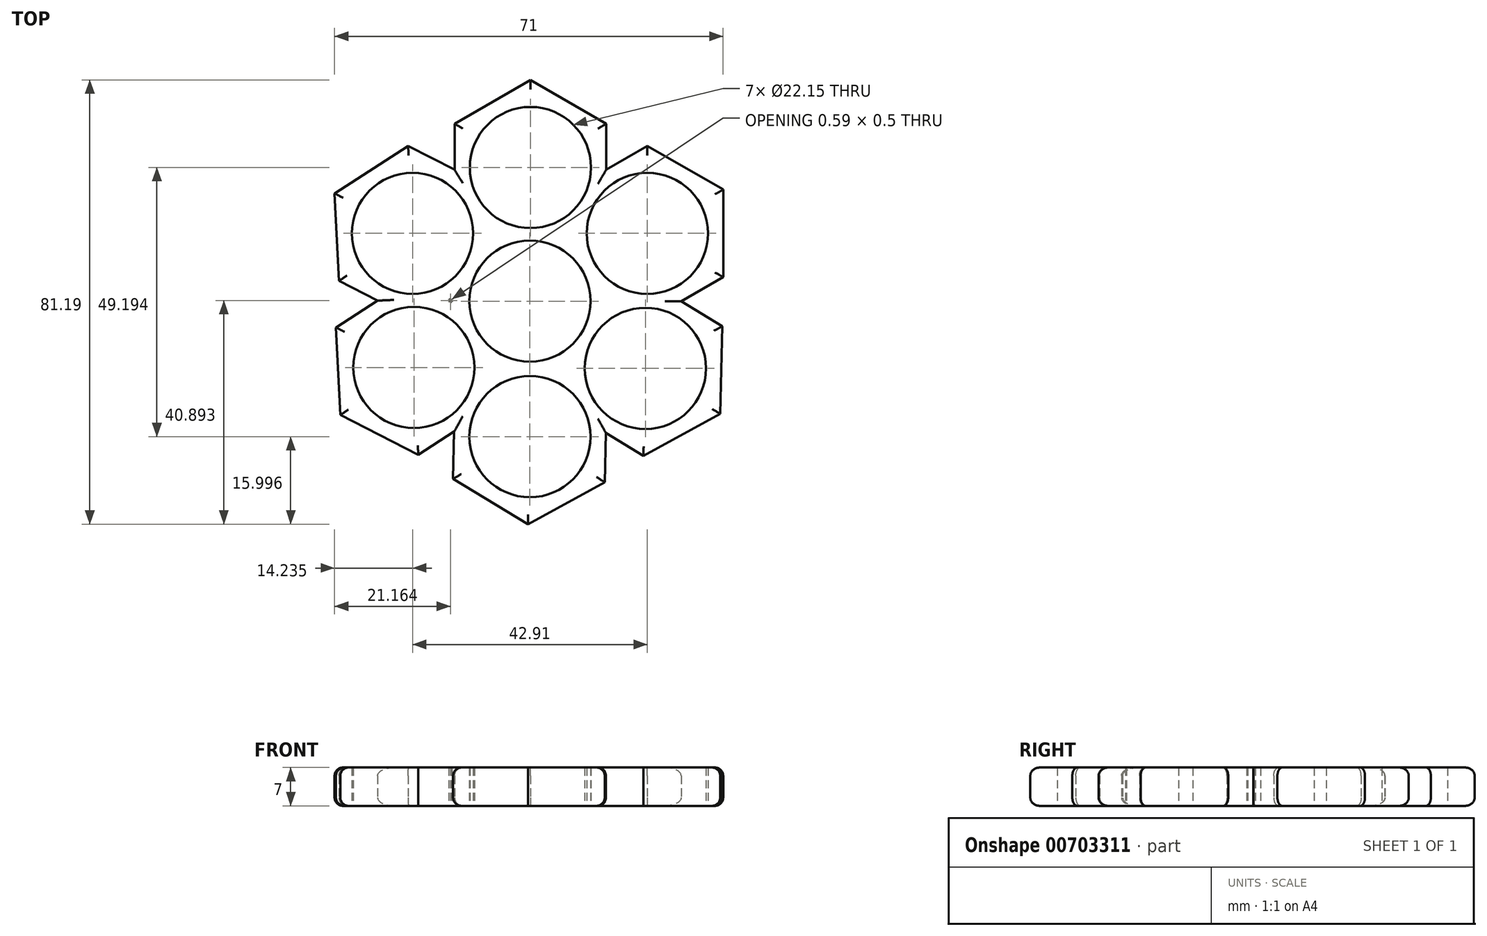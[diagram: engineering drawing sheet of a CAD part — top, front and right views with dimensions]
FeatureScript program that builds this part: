
annotation { "Feature Type Name" : "Feature", "Feature Type Description" : "" }
export const myFeature = defineFeature(function(context is Context, id is Id, definition is map)
    precondition{}
    {
        {
            var Q0;
            Q0=qCreatedBy(makeId("Top.planeOp"),FACE);
            var sketch = newSketch(context, id + "F0", { "sketchPlane" : qUnion([Q0])});
            skCircle(sketch, "E0.cCircle", {"center": v(0, 0) * mm, "radius": 12.21 * mm, "construction": true});
            skLineSegment(sketch, "E0.0", {"start": v(0.1, 24.42) * mm, "end": v(21.1, -12.3) * mm});
            skLineSegment(sketch, "E0.1", {"start": v(21.1, -12.3) * mm, "end": v(-21.2, -12.13) * mm});
            skLineSegment(sketch, "E0.2", {"start": v(-21.2, -12.13) * mm, "end": v(0.1, 24.42) * mm});
            skPoint(sketch, "E0.0.midPoint", {"position": v(10.6, 6.06) * mm});
            skCircle(sketch, "E1.cCircle", {"center": v(0.1, 24.42) * mm, "radius": 13.86 * mm, "construction": true});
            skLineSegment(sketch, "E1.0", {"start": v(13.95, 32.42) * mm, "end": v(13.95, 16.42) * mm});
            skLineSegment(sketch, "E1.1", {"start": v(13.95, 16.42) * mm, "end": v(0.1, 8.42) * mm});
            skLineSegment(sketch, "E1.2", {"start": v(0.1, 8.42) * mm, "end": v(-13.76, 16.42) * mm});
            skLineSegment(sketch, "E1.3", {"start": v(-13.76, 16.42) * mm, "end": v(-13.76, 32.42) * mm});
            skLineSegment(sketch, "E1.4", {"start": v(-13.76, 32.42) * mm, "end": v(0.1, 40.42) * mm});
            skLineSegment(sketch, "E1.5", {"start": v(0.1, 40.42) * mm, "end": v(13.95, 32.42) * mm});
            skPoint(sketch, "E1.0.midPoint", {"position": v(13.95, 24.42) * mm});
            skCircle(sketch, "E2.cCircle", {"center": v(21.1, -12.3) * mm, "radius": 13.86 * mm, "construction": true});
            skLineSegment(sketch, "E2.0", {"start": v(35.14, -4.61) * mm, "end": v(34.77, -20.6) * mm});
            skLineSegment(sketch, "E2.1", {"start": v(34.77, -20.6) * mm, "end": v(20.74, -28.29) * mm});
            skLineSegment(sketch, "E2.2", {"start": v(20.74, -28.29) * mm, "end": v(7.07, -19.98) * mm});
            skLineSegment(sketch, "E2.3", {"start": v(7.07, -19.98) * mm, "end": v(7.43, -3.98) * mm});
            skLineSegment(sketch, "E2.4", {"start": v(7.43, -3.98) * mm, "end": v(21.46, 3.7) * mm});
            skLineSegment(sketch, "E2.5", {"start": v(21.46, 3.7) * mm, "end": v(35.14, -4.61) * mm});
            skPoint(sketch, "E2.0.midPoint", {"position": v(34.95, -12.6) * mm});
            skCircle(sketch, "E3.cCircle", {"center": v(-21.2, -12.13) * mm, "radius": 13.86 * mm, "construction": true});
            skLineSegment(sketch, "E3.0", {"start": v(-20.4, -28.1) * mm, "end": v(-34.64, -20.8) * mm});
            skLineSegment(sketch, "E3.1", {"start": v(-34.64, -20.8) * mm, "end": v(-35.43, -4.83) * mm});
            skLineSegment(sketch, "E3.2", {"start": v(-35.43, -4.83) * mm, "end": v(-22, 3.85) * mm});
            skLineSegment(sketch, "E3.3", {"start": v(-22, 3.85) * mm, "end": v(-7.76, -3.45) * mm});
            skLineSegment(sketch, "E3.4", {"start": v(-7.76, -3.45) * mm, "end": v(-6.96, -19.43) * mm});
            skLineSegment(sketch, "E3.5", {"start": v(-6.96, -19.43) * mm, "end": v(-20.4, -28.1) * mm});
            skPoint(sketch, "E3.0.midPoint", {"position": v(-27.52, -24.46) * mm});
            skCircle(sketch, "E4", {"center": v(0.1, 24.42) * mm, "radius": 11.07 * mm});
            skCircle(sketch, "E5", {"center": v(0, 0) * mm, "radius": 11.07 * mm});
            skCircle(sketch, "E6", {"center": v(-21.2, -12.13) * mm, "radius": 11.07 * mm});
            skCircle(sketch, "E7", {"center": v(21.1, -12.3) * mm, "radius": 11.07 * mm});
            skCircle(sketch, "E8.cCircle", {"center": v(0, 0) * mm, "radius": 12.39 * mm, "construction": true});
            skLineSegment(sketch, "E8.0", {"start": v(21.45, 12.39) * mm, "end": v(0, -24.77) * mm});
            skLineSegment(sketch, "E8.1", {"start": v(0, -24.77) * mm, "end": v(-21.45, 12.39) * mm});
            skLineSegment(sketch, "E8.2", {"start": v(-21.45, 12.39) * mm, "end": v(21.45, 12.39) * mm});
            skPoint(sketch, "E8.0.midPoint", {"position": v(10.73, -6.2) * mm});
            skCircle(sketch, "E9.cCircle", {"center": v(21.45, 12.39) * mm, "radius": 13.86 * mm, "construction": true});
            skLineSegment(sketch, "E9.0", {"start": v(35.31, 4.39) * mm, "end": v(21.45, -3.61) * mm});
            skLineSegment(sketch, "E9.1", {"start": v(21.45, -3.61) * mm, "end": v(7.6, 4.39) * mm});
            skLineSegment(sketch, "E9.2", {"start": v(7.6, 4.39) * mm, "end": v(7.6, 20.39) * mm});
            skLineSegment(sketch, "E9.3", {"start": v(7.6, 20.39) * mm, "end": v(21.45, 28.39) * mm});
            skLineSegment(sketch, "E9.4", {"start": v(21.45, 28.39) * mm, "end": v(35.31, 20.39) * mm});
            skLineSegment(sketch, "E9.5", {"start": v(35.31, 20.39) * mm, "end": v(35.31, 4.39) * mm});
            skPoint(sketch, "E9.0.midPoint", {"position": v(28.38, 0.39) * mm});
            skCircle(sketch, "E10.cCircle", {"center": v(0, -24.77) * mm, "radius": 13.86 * mm, "construction": true});
            skLineSegment(sketch, "E10.0", {"start": v(13.67, -33.09) * mm, "end": v(-0.36, -40.77) * mm});
            skLineSegment(sketch, "E10.1", {"start": v(-0.36, -40.77) * mm, "end": v(-14.03, -32.46) * mm});
            skLineSegment(sketch, "E10.2", {"start": v(-14.03, -32.46) * mm, "end": v(-13.67, -16.46) * mm});
            skLineSegment(sketch, "E10.3", {"start": v(-13.67, -16.46) * mm, "end": v(0.36, -8.78) * mm});
            skLineSegment(sketch, "E10.4", {"start": v(0.36, -8.78) * mm, "end": v(14.03, -17.1) * mm});
            skLineSegment(sketch, "E10.5", {"start": v(14.03, -17.1) * mm, "end": v(13.67, -33.09) * mm});
            skPoint(sketch, "E10.0.midPoint", {"position": v(6.65, -36.93) * mm});
            skCircle(sketch, "E11.cCircle", {"center": v(-21.45, 12.39) * mm, "radius": 13.86 * mm, "construction": true});
            skLineSegment(sketch, "E11.0", {"start": v(-34.9, 3.7) * mm, "end": v(-35.7, 19.69) * mm});
            skLineSegment(sketch, "E11.1", {"start": v(-35.7, 19.69) * mm, "end": v(-22.25, 28.37) * mm});
            skLineSegment(sketch, "E11.2", {"start": v(-22.25, 28.37) * mm, "end": v(-8.01, 21.07) * mm});
            skLineSegment(sketch, "E11.3", {"start": v(-8.01, 21.07) * mm, "end": v(-7.22, 5.09) * mm});
            skLineSegment(sketch, "E11.4", {"start": v(-7.22, 5.09) * mm, "end": v(-20.66, -3.6) * mm});
            skLineSegment(sketch, "E11.5", {"start": v(-20.66, -3.6) * mm, "end": v(-34.9, 3.7) * mm});
            skPoint(sketch, "E11.0.midPoint", {"position": v(-35.3, 11.7) * mm});
            skCircle(sketch, "E12", {"center": v(21.45, 12.39) * mm, "radius": 11.07 * mm});
            skCircle(sketch, "E13", {"center": v(-21.45, 12.39) * mm, "radius": 11.07 * mm});
            skCircle(sketch, "E14", {"center": v(0, -24.77) * mm, "radius": 11.07 * mm});
            skSolve(sketch);
        }
        {
            var Q0;
            {var subQ16=sQuery(id+"F0.wireOp",EDGE,"E11.0");Q0=makeQuery(id+"F0.imprint","IMPRINT",FACE,{"disambiguationData":[TD([[makeQuery(id+"F0.imprint","IMPRINT",EDGE,{"derivedFrom":subQ16}),-1.0]])]});}
            var Q1;
            {var subQ7=sQuery(id+"F0.wireOp",EDGE,"E0.2");var subQ9=sQuery(id+"F0.wireOp",EDGE,"E11.4");var subQ11=makeQuery(id+"F0.imprint","INTERSECT",VERTEX,{"derivedFrom":[subQ7,subQ9]});Q1=makeQuery(id+"F0.imprint","IMPRINT",FACE,{"disambiguationData":[TD([[makeQuery(id+"F0.imprint","IMPRINT",EDGE,{"disambiguationData":[TD([[subQ11,-1.0]])],"derivedFrom":subQ7}),1.0]])]});}
            var Q2;
            {var subQ6=sQuery(id+"F0.wireOp",EDGE,"E1.4");Q2=makeQuery(id+"F0.imprint","IMPRINT",FACE,{"disambiguationData":[TD([[makeQuery(id+"F0.imprint","IMPRINT",EDGE,{"derivedFrom":subQ6}),-1.0]])]});}
            var Q3;
            {var subQ5=sQuery(id+"F0.wireOp",EDGE,"E4");var subQ6=sQuery(id+"F0.wireOp",EDGE,"E0.0");var subQ7=makeQuery(id+"F0.imprint","INTERSECT",VERTEX,{"derivedFrom":[subQ6,subQ5]});Q3=makeQuery(id+"F0.imprint","IMPRINT",FACE,{"disambiguationData":[TD([[makeQuery(id+"F0.imprint","IMPRINT",EDGE,{"disambiguationData":[TD([[subQ7,-1.0]])],"derivedFrom":subQ6}),-1.0]])]});}
            var Q4;
            Q4=makeQuery(id+"F0.imprint","IMPRINT",FACE,{"disambiguationData":[TD([[makeQuery(id+"F0.imprint","IMPRINT",EDGE,{"derivedFrom":sQuery(id+"F0.wireOp",EDGE,"E5")}),-1.0]])]});
            var Q5;
            {var subQ0=sQuery(id+"F0.wireOp",EDGE,"E1.1");var subQ1=sQuery(id+"F0.wireOp",EDGE,"E0.0");var subQ2=makeQuery(id+"F0.imprint","INTERSECT",VERTEX,{"derivedFrom":[subQ1,subQ0]});Q5=makeQuery(id+"F0.imprint","IMPRINT",FACE,{"disambiguationData":[TD([[makeQuery(id+"F0.imprint","IMPRINT",EDGE,{"disambiguationData":[TD([[subQ2,-1.0]])],"derivedFrom":subQ1}),1.0]])]});}
            var Q6;
            {var subQ1=sQuery(id+"F0.wireOp",EDGE,"E0.0");var subQ7=sQuery(id+"F0.wireOp",EDGE,"E9.2");var subQ8=makeQuery(id+"F0.imprint","INTERSECT",VERTEX,{"derivedFrom":[subQ1,subQ7]});Q6=makeQuery(id+"F0.imprint","IMPRINT",FACE,{"disambiguationData":[TD([[makeQuery(id+"F0.imprint","IMPRINT",EDGE,{"disambiguationData":[TD([[subQ8,-1.0]])],"derivedFrom":subQ1}),1.0]])]});}
            var Q7;
            {var subQ21=sQuery(id+"F0.wireOp",EDGE,"E9.4");Q7=makeQuery(id+"F0.imprint","IMPRINT",FACE,{"disambiguationData":[TD([[makeQuery(id+"F0.imprint","IMPRINT",EDGE,{"derivedFrom":subQ21}),-1.0]])]});}
            var Q8;
            {var subQ5=sQuery(id+"F0.wireOp",EDGE,"E11.5");var subQ9=sQuery(id+"F0.wireOp",EDGE,"E3.2");var subQ10=makeQuery(id+"F0.imprint","INTERSECT",VERTEX,{"derivedFrom":[subQ9,subQ5]});Q8=makeQuery(id+"F0.imprint","IMPRINT",FACE,{"disambiguationData":[TD([[makeQuery(id+"F0.imprint","IMPRINT",EDGE,{"disambiguationData":[TD([[subQ10,-1.0]])],"derivedFrom":subQ9}),-1.0]])]});}
            var Q9;
            {var subQ0=sQuery(id+"F0.wireOp",EDGE,"E13");var subQ1=sQuery(id+"F0.wireOp",EDGE,"E3.3");var subQ2=makeQuery(id+"F0.imprint","INTERSECT",VERTEX,{"derivedFrom":[subQ1,subQ0]});Q9=makeQuery(id+"F0.imprint","IMPRINT",FACE,{"disambiguationData":[TD([[makeQuery(id+"F0.imprint","IMPRINT",EDGE,{"disambiguationData":[TD([[subQ2,-1.0]])],"derivedFrom":subQ1}),1.0]])]});}
            var Q10;
            {var subQ0=sQuery(id+"F0.wireOp",EDGE,"E11.4");var subQ1=sQuery(id+"F0.wireOp",EDGE,"E0.2");var subQ2=makeQuery(id+"F0.imprint","INTERSECT",VERTEX,{"derivedFrom":[subQ1,subQ0]});Q10=makeQuery(id+"F0.imprint","IMPRINT",FACE,{"disambiguationData":[TD([[makeQuery(id+"F0.imprint","IMPRINT",EDGE,{"disambiguationData":[TD([[subQ2,-1.0]])],"derivedFrom":subQ1}),-1.0]])]});}
            var Q11;
            {var subQ0=sQuery(id+"F0.wireOp",EDGE,"E8.2");var subQ1=sQuery(id+"F0.wireOp",EDGE,"E0.2");var subQ2=makeQuery(id+"F0.imprint","INTERSECT",VERTEX,{"derivedFrom":[subQ1,subQ0]});Q11=makeQuery(id+"F0.imprint","IMPRINT",FACE,{"disambiguationData":[TD([[makeQuery(id+"F0.imprint","IMPRINT",EDGE,{"disambiguationData":[TD([[subQ2,-1.0]])],"derivedFrom":subQ1}),1.0]])]});}
            var Q12;
            {var subQ0=sQuery(id+"F0.wireOp",EDGE,"E8.2");var subQ1=sQuery(id+"F0.wireOp",EDGE,"E0.0");var subQ2=makeQuery(id+"F0.imprint","INTERSECT",VERTEX,{"derivedFrom":[subQ1,subQ0]});Q12=makeQuery(id+"F0.imprint","IMPRINT",FACE,{"disambiguationData":[TD([[makeQuery(id+"F0.imprint","IMPRINT",EDGE,{"disambiguationData":[TD([[subQ2,-1.0]])],"derivedFrom":subQ1}),1.0]])]});}
            var Q13;
            {var subQ0=sQuery(id+"F0.wireOp",EDGE,"E1.1");var subQ1=sQuery(id+"F0.wireOp",EDGE,"E0.0");var subQ2=makeQuery(id+"F0.imprint","INTERSECT",VERTEX,{"derivedFrom":[subQ1,subQ0]});Q13=makeQuery(id+"F0.imprint","IMPRINT",FACE,{"disambiguationData":[TD([[makeQuery(id+"F0.imprint","IMPRINT",EDGE,{"disambiguationData":[TD([[subQ2,-1.0]])],"derivedFrom":subQ1}),-1.0]])]});}
            var Q14;
            {var subQ0=sQuery(id+"F0.wireOp",EDGE,"E8.2");var subQ1=sQuery(id+"F0.wireOp",EDGE,"E0.2");var subQ2=makeQuery(id+"F0.imprint","INTERSECT",VERTEX,{"derivedFrom":[subQ1,subQ0]});Q14=makeQuery(id+"F0.imprint","IMPRINT",FACE,{"disambiguationData":[TD([[makeQuery(id+"F0.imprint","IMPRINT",EDGE,{"disambiguationData":[TD([[subQ2,-1.0]])],"derivedFrom":subQ1}),-1.0]])]});}
            var Q15;
            {var subQ0=sQuery(id+"F0.wireOp",EDGE,"E11.3");var subQ1=sQuery(id+"F0.wireOp",EDGE,"E0.2");var subQ2=makeQuery(id+"F0.imprint","INTERSECT",VERTEX,{"derivedFrom":[subQ1,subQ0]});Q15=makeQuery(id+"F0.imprint","IMPRINT",FACE,{"disambiguationData":[TD([[makeQuery(id+"F0.imprint","IMPRINT",EDGE,{"disambiguationData":[TD([[subQ2,-1.0]])],"derivedFrom":subQ1}),1.0]])]});}
            var Q16;
            {var subQ0=sQuery(id+"F0.wireOp",EDGE,"E9.2");var subQ1=sQuery(id+"F0.wireOp",EDGE,"E0.0");var subQ2=makeQuery(id+"F0.imprint","INTERSECT",VERTEX,{"derivedFrom":[subQ1,subQ0]});Q16=makeQuery(id+"F0.imprint","IMPRINT",FACE,{"disambiguationData":[TD([[makeQuery(id+"F0.imprint","IMPRINT",EDGE,{"disambiguationData":[TD([[subQ2,-1.0]])],"derivedFrom":subQ1}),-1.0]])]});}
            var Q17;
            {var subQ0=sQuery(id+"F0.wireOp",EDGE,"E9.1");var subQ1=sQuery(id+"F0.wireOp",EDGE,"E0.0");var subQ2=makeQuery(id+"F0.imprint","INTERSECT",VERTEX,{"derivedFrom":[subQ1,subQ0]});Q17=makeQuery(id+"F0.imprint","IMPRINT",FACE,{"disambiguationData":[TD([[makeQuery(id+"F0.imprint","IMPRINT",EDGE,{"disambiguationData":[TD([[subQ2,-1.0]])],"derivedFrom":subQ1}),1.0]])]});}
            var Q18;
            {var subQ0=sQuery(id+"F0.wireOp",EDGE,"E2.4");var subQ1=sQuery(id+"F0.wireOp",EDGE,"E0.0");var subQ2=makeQuery(id+"F0.imprint","INTERSECT",VERTEX,{"derivedFrom":[subQ1,subQ0]});Q18=makeQuery(id+"F0.imprint","IMPRINT",FACE,{"disambiguationData":[TD([[makeQuery(id+"F0.imprint","IMPRINT",EDGE,{"disambiguationData":[TD([[subQ2,-1.0]])],"derivedFrom":subQ1}),-1.0]])]});}
            var Q19;
            {var subQ15=sQuery(id+"F0.wireOp",EDGE,"E2.0");Q19=makeQuery(id+"F0.imprint","IMPRINT",FACE,{"disambiguationData":[TD([[makeQuery(id+"F0.imprint","IMPRINT",EDGE,{"derivedFrom":subQ15}),-1.0]])]});}
            var Q20;
            {var subQ0=sQuery(id+"F0.wireOp",EDGE,"E8.0");var subQ1=sQuery(id+"F0.wireOp",EDGE,"E0.0");var subQ2=makeQuery(id+"F0.imprint","INTERSECT",VERTEX,{"derivedFrom":[subQ1,subQ0]});Q20=makeQuery(id+"F0.imprint","IMPRINT",FACE,{"disambiguationData":[TD([[makeQuery(id+"F0.imprint","IMPRINT",EDGE,{"disambiguationData":[TD([[subQ2,-1.0]])],"derivedFrom":subQ1}),-1.0]])]});}
            var Q21;
            {var subQ0=sQuery(id+"F0.wireOp",EDGE,"E8.1");var subQ1=sQuery(id+"F0.wireOp",EDGE,"E0.2");var subQ2=makeQuery(id+"F0.imprint","INTERSECT",VERTEX,{"derivedFrom":[subQ1,subQ0]});Q21=makeQuery(id+"F0.imprint","IMPRINT",FACE,{"disambiguationData":[TD([[makeQuery(id+"F0.imprint","IMPRINT",EDGE,{"disambiguationData":[TD([[subQ2,-1.0]])],"derivedFrom":subQ1}),1.0]])]});}
            var Q22;
            {var subQ0=sQuery(id+"F0.wireOp",EDGE,"E3.3");var subQ1=sQuery(id+"F0.wireOp",EDGE,"E0.2");var subQ2=makeQuery(id+"F0.imprint","INTERSECT",VERTEX,{"derivedFrom":[subQ1,subQ0]});Q22=makeQuery(id+"F0.imprint","IMPRINT",FACE,{"disambiguationData":[TD([[makeQuery(id+"F0.imprint","IMPRINT",EDGE,{"disambiguationData":[TD([[subQ2,-1.0]])],"derivedFrom":subQ1}),1.0]])]});}
            var Q23;
            {var subQ0=sQuery(id+"F0.wireOp",EDGE,"E3.3");var subQ1=sQuery(id+"F0.wireOp",EDGE,"E0.2");var subQ2=makeQuery(id+"F0.imprint","INTERSECT",VERTEX,{"derivedFrom":[subQ1,subQ0]});Q23=makeQuery(id+"F0.imprint","IMPRINT",FACE,{"disambiguationData":[TD([[makeQuery(id+"F0.imprint","IMPRINT",EDGE,{"disambiguationData":[TD([[subQ2,-1.0]])],"derivedFrom":subQ1}),-1.0]])]});}
            var Q24;
            {var subQ7=sQuery(id+"F0.wireOp",EDGE,"E3.4");var subQ8=sQuery(id+"F0.wireOp",EDGE,"E0.1");var subQ9=makeQuery(id+"F0.imprint","INTERSECT",VERTEX,{"derivedFrom":[subQ8,subQ7]});Q24=makeQuery(id+"F0.imprint","IMPRINT",FACE,{"disambiguationData":[TD([[makeQuery(id+"F0.imprint","IMPRINT",EDGE,{"disambiguationData":[TD([[subQ9,-1.0]])],"derivedFrom":subQ8}),-1.0]])]});}
            var Q25;
            {var subQ0=sQuery(id+"F0.wireOp",EDGE,"E6");var subQ1=sQuery(id+"F0.wireOp",EDGE,"E0.2");var subQ2=makeQuery(id+"F0.imprint","INTERSECT",VERTEX,{"derivedFrom":[subQ1,subQ0]});Q25=makeQuery(id+"F0.imprint","IMPRINT",FACE,{"disambiguationData":[TD([[makeQuery(id+"F0.imprint","IMPRINT",EDGE,{"disambiguationData":[TD([[subQ2,-1.0]])],"derivedFrom":subQ1}),1.0]])]});}
            var Q26;
            {var subQ9=sQuery(id+"F0.wireOp",EDGE,"E3.0");Q26=makeQuery(id+"F0.imprint","IMPRINT",FACE,{"disambiguationData":[TD([[makeQuery(id+"F0.imprint","IMPRINT",EDGE,{"derivedFrom":subQ9}),-1.0]])]});}
            var Q27;
            {var subQ0=sQuery(id+"F0.wireOp",EDGE,"E8.1");var subQ1=sQuery(id+"F0.wireOp",EDGE,"E0.1");var subQ2=makeQuery(id+"F0.imprint","INTERSECT",VERTEX,{"derivedFrom":[subQ1,subQ0]});Q27=makeQuery(id+"F0.imprint","IMPRINT",FACE,{"disambiguationData":[TD([[makeQuery(id+"F0.imprint","IMPRINT",EDGE,{"disambiguationData":[TD([[subQ2,-1.0]])],"derivedFrom":subQ1}),-1.0]])]});}
            var Q28;
            {var subQ0=sQuery(id+"F0.wireOp",EDGE,"E2.3");var subQ1=sQuery(id+"F0.wireOp",EDGE,"E0.1");var subQ2=makeQuery(id+"F0.imprint","INTERSECT",VERTEX,{"derivedFrom":[subQ1,subQ0]});Q28=makeQuery(id+"F0.imprint","IMPRINT",FACE,{"disambiguationData":[TD([[makeQuery(id+"F0.imprint","IMPRINT",EDGE,{"disambiguationData":[TD([[subQ2,-1.0]])],"derivedFrom":subQ1}),1.0]])]});}
            var Q29;
            {var subQ0=sQuery(id+"F0.wireOp",EDGE,"E2.3");var subQ1=sQuery(id+"F0.wireOp",EDGE,"E0.1");var subQ2=makeQuery(id+"F0.imprint","INTERSECT",VERTEX,{"derivedFrom":[subQ1,subQ0]});Q29=makeQuery(id+"F0.imprint","IMPRINT",FACE,{"disambiguationData":[TD([[makeQuery(id+"F0.imprint","IMPRINT",EDGE,{"disambiguationData":[TD([[subQ2,-1.0]])],"derivedFrom":subQ1}),-1.0]])]});}
            var Q30;
            {var subQ0=sQuery(id+"F0.wireOp",EDGE,"E8.0");var subQ1=sQuery(id+"F0.wireOp",EDGE,"E0.1");var subQ2=makeQuery(id+"F0.imprint","INTERSECT",VERTEX,{"derivedFrom":[subQ1,subQ0]});Q30=makeQuery(id+"F0.imprint","IMPRINT",FACE,{"disambiguationData":[TD([[makeQuery(id+"F0.imprint","IMPRINT",EDGE,{"disambiguationData":[TD([[subQ2,-1.0]])],"derivedFrom":subQ1}),1.0]])]});}
            var Q31;
            {var subQ0=sQuery(id+"F0.wireOp",EDGE,"E8.1");var subQ1=sQuery(id+"F0.wireOp",EDGE,"E0.1");var subQ2=makeQuery(id+"F0.imprint","INTERSECT",VERTEX,{"derivedFrom":[subQ1,subQ0]});Q31=makeQuery(id+"F0.imprint","IMPRINT",FACE,{"disambiguationData":[TD([[makeQuery(id+"F0.imprint","IMPRINT",EDGE,{"disambiguationData":[TD([[subQ2,-1.0]])],"derivedFrom":subQ1}),1.0]])]});}
            var Q32;
            {var subQ5=sQuery(id+"F0.wireOp",EDGE,"E0.1");var subQ7=sQuery(id+"F0.wireOp",EDGE,"E10.4");var subQ11=makeQuery(id+"F0.imprint","INTERSECT",VERTEX,{"derivedFrom":[subQ5,subQ7]});Q32=makeQuery(id+"F0.imprint","IMPRINT",FACE,{"disambiguationData":[TD([[makeQuery(id+"F0.imprint","IMPRINT",EDGE,{"disambiguationData":[TD([[subQ11,-1.0]])],"derivedFrom":subQ5}),1.0]])]});}
            var Q33;
            {var subQ0=sQuery(id+"F0.wireOp",EDGE,"E10.4");var subQ1=sQuery(id+"F0.wireOp",EDGE,"E0.1");var subQ2=makeQuery(id+"F0.imprint","INTERSECT",VERTEX,{"derivedFrom":[subQ1,subQ0]});Q33=makeQuery(id+"F0.imprint","IMPRINT",FACE,{"disambiguationData":[TD([[makeQuery(id+"F0.imprint","IMPRINT",EDGE,{"disambiguationData":[TD([[subQ2,-1.0]])],"derivedFrom":subQ1}),-1.0]])]});}
            var Q34;
            {var subQ5=sQuery(id+"F0.wireOp",EDGE,"E10.0");Q34=makeQuery(id+"F0.imprint","IMPRINT",FACE,{"disambiguationData":[TD([[makeQuery(id+"F0.imprint","IMPRINT",EDGE,{"derivedFrom":subQ5}),-1.0]])]});}
            var Q35;
            {var subQ0=sQuery(id+"F0.wireOp",EDGE,"E10.3");var subQ1=sQuery(id+"F0.wireOp",EDGE,"E0.1");var subQ2=makeQuery(id+"F0.imprint","INTERSECT",VERTEX,{"derivedFrom":[subQ1,subQ0]});Q35=makeQuery(id+"F0.imprint","IMPRINT",FACE,{"disambiguationData":[TD([[makeQuery(id+"F0.imprint","IMPRINT",EDGE,{"disambiguationData":[TD([[subQ2,-1.0]])],"derivedFrom":subQ1}),1.0]])]});}
            var Q36;
            {var subQ9=sQuery(id+"F0.wireOp",EDGE,"E8.2");var subQ10=sQuery(id+"F0.wireOp",EDGE,"E1.2");var subQ11=makeQuery(id+"F0.imprint","INTERSECT",VERTEX,{"derivedFrom":[subQ10,subQ9]});Q36=makeQuery(id+"F0.imprint","IMPRINT",FACE,{"disambiguationData":[TD([[makeQuery(id+"F0.imprint","IMPRINT",EDGE,{"disambiguationData":[TD([[subQ11,-1.0]])],"derivedFrom":subQ10}),-1.0]])]});}
            var Q37;
            {var subQ8=sQuery(id+"F0.wireOp",EDGE,"E8.2");var subQ10=sQuery(id+"F0.wireOp",EDGE,"E0.0");var subQ11=makeQuery(id+"F0.imprint","INTERSECT",VERTEX,{"derivedFrom":[subQ10,subQ8]});Q37=makeQuery(id+"F0.imprint","IMPRINT",FACE,{"disambiguationData":[TD([[makeQuery(id+"F0.imprint","IMPRINT",EDGE,{"disambiguationData":[TD([[subQ11,-1.0]])],"derivedFrom":subQ10}),-1.0]])]});}
            var Q38;
            {var subQ7=sQuery(id+"F0.wireOp",EDGE,"E9.3");var subQ11=sQuery(id+"F0.wireOp",EDGE,"E1.0");var subQ12=makeQuery(id+"F0.imprint","INTERSECT",VERTEX,{"derivedFrom":[subQ11,subQ7]});Q38=makeQuery(id+"F0.imprint","IMPRINT",FACE,{"disambiguationData":[TD([[makeQuery(id+"F0.imprint","IMPRINT",EDGE,{"disambiguationData":[TD([[subQ12,-1.0]])],"derivedFrom":subQ11}),-1.0]])]});}
            var Q39;
            {var subQ9=sQuery(id+"F0.wireOp",EDGE,"E8.0");var subQ10=sQuery(id+"F0.wireOp",EDGE,"E2.4");var subQ11=makeQuery(id+"F0.imprint","INTERSECT",VERTEX,{"derivedFrom":[subQ10,subQ9]});Q39=makeQuery(id+"F0.imprint","IMPRINT",FACE,{"disambiguationData":[TD([[makeQuery(id+"F0.imprint","IMPRINT",EDGE,{"disambiguationData":[TD([[subQ11,-1.0]])],"derivedFrom":subQ10}),-1.0]])]});}
            var Q40;
            {var subQ0=sQuery(id+"F0.wireOp",EDGE,"E8.0");var subQ1=sQuery(id+"F0.wireOp",EDGE,"E2.4");var subQ2=makeQuery(id+"F0.imprint","INTERSECT",VERTEX,{"derivedFrom":[subQ1,subQ0]});Q40=makeQuery(id+"F0.imprint","IMPRINT",FACE,{"disambiguationData":[TD([[makeQuery(id+"F0.imprint","IMPRINT",EDGE,{"disambiguationData":[TD([[subQ2,-1.0]])],"derivedFrom":subQ1}),1.0]])]});}
            var Q41;
            {var subQ7=sQuery(id+"F0.wireOp",EDGE,"E10.5");var subQ11=sQuery(id+"F0.wireOp",EDGE,"E2.2");var subQ12=makeQuery(id+"F0.imprint","INTERSECT",VERTEX,{"derivedFrom":[subQ11,subQ7]});Q41=makeQuery(id+"F0.imprint","IMPRINT",FACE,{"disambiguationData":[TD([[makeQuery(id+"F0.imprint","IMPRINT",EDGE,{"disambiguationData":[TD([[subQ12,-1.0]])],"derivedFrom":subQ11}),-1.0]])]});}
            var Q42;
            {var subQ0=sQuery(id+"F0.wireOp",EDGE,"E8.1");var subQ1=sQuery(id+"F0.wireOp",EDGE,"E3.4");var subQ2=makeQuery(id+"F0.imprint","INTERSECT",VERTEX,{"derivedFrom":[subQ1,subQ0]});Q42=makeQuery(id+"F0.imprint","IMPRINT",FACE,{"disambiguationData":[TD([[makeQuery(id+"F0.imprint","IMPRINT",EDGE,{"disambiguationData":[TD([[subQ2,-1.0]])],"derivedFrom":subQ1}),-1.0]])]});}
            var Q43;
            {var subQ0=sQuery(id+"F0.wireOp",EDGE,"E9.1");var subQ1=sQuery(id+"F0.wireOp",EDGE,"E0.0");var subQ2=makeQuery(id+"F0.imprint","INTERSECT",VERTEX,{"derivedFrom":[subQ1,subQ0]});Q43=makeQuery(id+"F0.imprint","IMPRINT",FACE,{"disambiguationData":[TD([[makeQuery(id+"F0.imprint","IMPRINT",EDGE,{"disambiguationData":[TD([[subQ2,-1.0]])],"derivedFrom":subQ1}),-1.0]])]});}
            var Q44;
            {var subQ0=sQuery(id+"F0.wireOp",EDGE,"E10.3");var subQ1=sQuery(id+"F0.wireOp",EDGE,"E0.1");var subQ2=makeQuery(id+"F0.imprint","INTERSECT",VERTEX,{"derivedFrom":[subQ1,subQ0]});Q44=makeQuery(id+"F0.imprint","IMPRINT",FACE,{"disambiguationData":[TD([[makeQuery(id+"F0.imprint","IMPRINT",EDGE,{"disambiguationData":[TD([[subQ2,-1.0]])],"derivedFrom":subQ1}),-1.0]])]});}
            var Q45;
            {var subQ0=sQuery(id+"F0.wireOp",EDGE,"E7");var subQ1=sQuery(id+"F0.wireOp",EDGE,"E0.1");var subQ2=makeQuery(id+"F0.imprint","INTERSECT",VERTEX,{"derivedFrom":[subQ1,subQ0]});Q45=makeQuery(id+"F0.imprint","IMPRINT",FACE,{"disambiguationData":[TD([[makeQuery(id+"F0.imprint","IMPRINT",EDGE,{"disambiguationData":[TD([[subQ2,-1.0]])],"derivedFrom":subQ1}),1.0]])]});}
            var Q46;
            {var subQ0=sQuery(id+"F0.wireOp",EDGE,"E1.2");var subQ1=sQuery(id+"F0.wireOp",EDGE,"E0.2");var subQ2=makeQuery(id+"F0.imprint","INTERSECT",VERTEX,{"derivedFrom":[subQ1,subQ0]});Q46=makeQuery(id+"F0.imprint","IMPRINT",FACE,{"disambiguationData":[TD([[makeQuery(id+"F0.imprint","IMPRINT",EDGE,{"disambiguationData":[TD([[subQ2,-1.0]])],"derivedFrom":subQ1}),1.0]])]});}
            var Q47;
            {var subQ0=sQuery(id+"F0.wireOp",EDGE,"E4");var subQ1=sQuery(id+"F0.wireOp",EDGE,"E0.0");var subQ2=makeQuery(id+"F0.imprint","INTERSECT",VERTEX,{"derivedFrom":[subQ1,subQ0]});Q47=makeQuery(id+"F0.imprint","IMPRINT",FACE,{"disambiguationData":[TD([[makeQuery(id+"F0.imprint","IMPRINT",EDGE,{"disambiguationData":[TD([[subQ2,-1.0]])],"derivedFrom":subQ1}),1.0]])]});}
            var Q48;
            {var subQ0=sQuery(id+"F0.wireOp",EDGE,"E12");var subQ1=sQuery(id+"F0.wireOp",EDGE,"E1.1");var subQ2=makeQuery(id+"F0.imprint","INTERSECT",VERTEX,{"derivedFrom":[subQ1,subQ0]});Q48=makeQuery(id+"F0.imprint","IMPRINT",FACE,{"disambiguationData":[TD([[makeQuery(id+"F0.imprint","IMPRINT",EDGE,{"disambiguationData":[TD([[subQ2,-1.0]])],"derivedFrom":subQ1}),1.0]])]});}
            var Q49;
            {var subQ0=sQuery(id+"F0.wireOp",EDGE,"E9.1");var subQ1=sQuery(id+"F0.wireOp",EDGE,"E2.4");var subQ2=makeQuery(id+"F0.imprint","INTERSECT",VERTEX,{"derivedFrom":[subQ1,subQ0]});Q49=makeQuery(id+"F0.imprint","IMPRINT",FACE,{"disambiguationData":[TD([[makeQuery(id+"F0.imprint","IMPRINT",EDGE,{"disambiguationData":[TD([[subQ2,-1.0]])],"derivedFrom":subQ1}),-1.0]])]});}
            var Q50;
            {var subQ0=sQuery(id+"F0.wireOp",EDGE,"E8.0");var subQ1=sQuery(id+"F0.wireOp",EDGE,"E0.0");var subQ2=makeQuery(id+"F0.imprint","INTERSECT",VERTEX,{"derivedFrom":[subQ1,subQ0]});Q50=makeQuery(id+"F0.imprint","IMPRINT",FACE,{"disambiguationData":[TD([[makeQuery(id+"F0.imprint","IMPRINT",EDGE,{"disambiguationData":[TD([[subQ2,-1.0]])],"derivedFrom":subQ1}),1.0]])]});}
            var Q51;
            {var subQ0=sQuery(id+"F0.wireOp",EDGE,"E2.4");var subQ1=sQuery(id+"F0.wireOp",EDGE,"E0.0");var subQ2=makeQuery(id+"F0.imprint","INTERSECT",VERTEX,{"derivedFrom":[subQ1,subQ0]});Q51=makeQuery(id+"F0.imprint","IMPRINT",FACE,{"disambiguationData":[TD([[makeQuery(id+"F0.imprint","IMPRINT",EDGE,{"disambiguationData":[TD([[subQ2,-1.0]])],"derivedFrom":subQ1}),1.0]])]});}
            var Q52;
            {var subQ0=sQuery(id+"F0.wireOp",EDGE,"E1.2");var subQ1=sQuery(id+"F0.wireOp",EDGE,"E0.2");var subQ2=makeQuery(id+"F0.imprint","INTERSECT",VERTEX,{"derivedFrom":[subQ1,subQ0]});Q52=makeQuery(id+"F0.imprint","IMPRINT",FACE,{"disambiguationData":[TD([[makeQuery(id+"F0.imprint","IMPRINT",EDGE,{"disambiguationData":[TD([[subQ2,-1.0]])],"derivedFrom":subQ1}),-1.0]])]});}
            var Q53;
            {var subQ0=sQuery(id+"F0.wireOp",EDGE,"E8.2");var subQ1=sQuery(id+"F0.wireOp",EDGE,"E1.2");var subQ2=makeQuery(id+"F0.imprint","INTERSECT",VERTEX,{"derivedFrom":[subQ1,subQ0]});Q53=makeQuery(id+"F0.imprint","IMPRINT",FACE,{"disambiguationData":[TD([[makeQuery(id+"F0.imprint","IMPRINT",EDGE,{"disambiguationData":[TD([[subQ2,-1.0]])],"derivedFrom":subQ1}),1.0]])]});}
            var Q54;
            {var subQ0=sQuery(id+"F0.wireOp",EDGE,"E10.3");var subQ1=sQuery(id+"F0.wireOp",EDGE,"E3.4");var subQ2=makeQuery(id+"F0.imprint","INTERSECT",VERTEX,{"derivedFrom":[subQ1,subQ0]});Q54=makeQuery(id+"F0.imprint","IMPRINT",FACE,{"disambiguationData":[TD([[makeQuery(id+"F0.imprint","IMPRINT",EDGE,{"disambiguationData":[TD([[subQ2,-1.0]])],"derivedFrom":subQ1}),-1.0]])]});}
            var Q55;
            {var subQ0=sQuery(id+"F0.wireOp",EDGE,"E8.1");var subQ1=sQuery(id+"F0.wireOp",EDGE,"E3.4");var subQ2=makeQuery(id+"F0.imprint","INTERSECT",VERTEX,{"derivedFrom":[subQ1,subQ0]});Q55=makeQuery(id+"F0.imprint","IMPRINT",FACE,{"disambiguationData":[TD([[makeQuery(id+"F0.imprint","IMPRINT",EDGE,{"disambiguationData":[TD([[subQ2,-1.0]])],"derivedFrom":subQ1}),1.0]])]});}
            var Q56;
            {var subQ0=sQuery(id+"F0.wireOp",EDGE,"E3.4");var subQ1=sQuery(id+"F0.wireOp",EDGE,"E0.1");var subQ2=makeQuery(id+"F0.imprint","INTERSECT",VERTEX,{"derivedFrom":[subQ1,subQ0]});Q56=makeQuery(id+"F0.imprint","IMPRINT",FACE,{"disambiguationData":[TD([[makeQuery(id+"F0.imprint","IMPRINT",EDGE,{"disambiguationData":[TD([[subQ2,-1.0]])],"derivedFrom":subQ1}),1.0]])]});}
            var Q57;
            {var subQ0=sQuery(id+"F0.wireOp",EDGE,"E14");var subQ1=sQuery(id+"F0.wireOp",EDGE,"E2.3");var subQ2=makeQuery(id+"F0.imprint","INTERSECT",VERTEX,{"derivedFrom":[subQ1,subQ0]});Q57=makeQuery(id+"F0.imprint","IMPRINT",FACE,{"disambiguationData":[TD([[makeQuery(id+"F0.imprint","IMPRINT",EDGE,{"disambiguationData":[TD([[subQ2,-1.0]])],"derivedFrom":subQ1}),1.0]])]});}
            var Q58;
            {var subQ0=sQuery(id+"F0.wireOp",EDGE,"E11.3");var subQ9=sQuery(id+"F0.wireOp",EDGE,"E1.2");var subQ10=makeQuery(id+"F0.imprint","INTERSECT",VERTEX,{"derivedFrom":[subQ9,subQ0]});Q58=makeQuery(id+"F0.imprint","IMPRINT",FACE,{"disambiguationData":[TD([[makeQuery(id+"F0.imprint","IMPRINT",EDGE,{"disambiguationData":[TD([[subQ10,-1.0]])],"derivedFrom":subQ9}),-1.0]])]});}
            var Q59;
            {var subQ0=sQuery(id+"F0.wireOp",EDGE,"E11.3");var subQ1=sQuery(id+"F0.wireOp",EDGE,"E1.2");var subQ2=makeQuery(id+"F0.imprint","INTERSECT",VERTEX,{"derivedFrom":[subQ1,subQ0]});Q59=makeQuery(id+"F0.imprint","IMPRINT",FACE,{"disambiguationData":[TD([[makeQuery(id+"F0.imprint","IMPRINT",EDGE,{"disambiguationData":[TD([[subQ2,-1.0]])],"derivedFrom":subQ1}),1.0]])]});}
            var Q60;
            {var subQ0=sQuery(id+"F0.wireOp",EDGE,"E11.3");var subQ1=sQuery(id+"F0.wireOp",EDGE,"E0.2");var subQ2=makeQuery(id+"F0.imprint","INTERSECT",VERTEX,{"derivedFrom":[subQ1,subQ0]});Q60=makeQuery(id+"F0.imprint","IMPRINT",FACE,{"disambiguationData":[TD([[makeQuery(id+"F0.imprint","IMPRINT",EDGE,{"disambiguationData":[TD([[subQ2,-1.0]])],"derivedFrom":subQ1}),-1.0]])]});}
            var Q61;
            {var subQ1=sQuery(id+"F0.wireOp",EDGE,"E0.2");var subQ5=sQuery(id+"F0.wireOp",EDGE,"E8.1");var subQ6=makeQuery(id+"F0.imprint","INTERSECT",VERTEX,{"derivedFrom":[subQ1,subQ5]});Q61=makeQuery(id+"F0.imprint","IMPRINT",FACE,{"disambiguationData":[TD([[makeQuery(id+"F0.imprint","IMPRINT",EDGE,{"disambiguationData":[TD([[subQ6,-1.0]])],"derivedFrom":subQ1}),-1.0]])]});}
            var Q62;
            {var subQ1=sQuery(id+"F0.wireOp",EDGE,"E0.1");var subQ5=sQuery(id+"F0.wireOp",EDGE,"E8.0");var subQ6=makeQuery(id+"F0.imprint","INTERSECT",VERTEX,{"derivedFrom":[subQ1,subQ5]});Q62=makeQuery(id+"F0.imprint","IMPRINT",FACE,{"disambiguationData":[TD([[makeQuery(id+"F0.imprint","IMPRINT",EDGE,{"disambiguationData":[TD([[subQ6,-1.0]])],"derivedFrom":subQ1}),-1.0]])]});}
            var Q63;
            {var subQ0=sQuery(id+"F0.wireOp",EDGE,"E10.3");var subQ1=sQuery(id+"F0.wireOp",EDGE,"E3.4");var subQ2=makeQuery(id+"F0.imprint","INTERSECT",VERTEX,{"derivedFrom":[subQ1,subQ0]});Q63=makeQuery(id+"F0.imprint","IMPRINT",FACE,{"disambiguationData":[TD([[makeQuery(id+"F0.imprint","IMPRINT",EDGE,{"disambiguationData":[TD([[subQ2,-1.0]])],"derivedFrom":subQ1}),1.0]])]});}
            var Q64;
            {var subQ0=sQuery(id+"F0.wireOp",EDGE,"E9.1");var subQ1=sQuery(id+"F0.wireOp",EDGE,"E2.4");var subQ2=makeQuery(id+"F0.imprint","INTERSECT",VERTEX,{"derivedFrom":[subQ1,subQ0]});Q64=makeQuery(id+"F0.imprint","IMPRINT",FACE,{"disambiguationData":[TD([[makeQuery(id+"F0.imprint","IMPRINT",EDGE,{"disambiguationData":[TD([[subQ2,-1.0]])],"derivedFrom":subQ1}),1.0]])]});}
            extrude(context, id + "F1", {"entities" : qUnion([Q0, Q1, Q2, Q3, Q4, Q5, Q6, Q7, Q8, Q9, Q10, Q11, Q12, Q13, Q14, Q15, Q16, Q17, Q18, Q19, Q20, Q21, Q22, Q23, Q24, Q25, Q26, Q27, Q28, Q29, Q30, Q31, Q32, Q33, Q34, Q35, Q36, Q37, Q38, Q39, Q40, Q41, Q42, Q43, Q44, Q45, Q46, Q47, Q48, Q49, Q50, Q51, Q52, Q53, Q54, Q55, Q56, Q57, Q58, Q59, Q60, Q61, Q62, Q63, Q64]), "depth" : 7 * mm, "offsetDistance" : 25 * mm});
        }
        {
            var Q0;
            Q0=makeQuery(id+"F1.opExtrude","CAP_EDGE",EDGE,{"disambiguationData":[OSD([sQuery(id+"F0.wireOp",EDGE,"E11.5")])],"isStart":true});
            var Q1;
            Q1=makeQuery(id+"F1.opExtrude","CAP_EDGE",EDGE,{"disambiguationData":[OSD([sQuery(id+"F0.wireOp",EDGE,"E3.2")])],"isStart":true});
            var Q2;
            Q2=makeQuery(id+"F1.opExtrude","CAP_EDGE",EDGE,{"disambiguationData":[OSD([sQuery(id+"F0.wireOp",EDGE,"E3.1")])],"isStart":true});
            var Q3;
            Q3=makeQuery(id+"F1.opExtrude","CAP_EDGE",EDGE,{"disambiguationData":[OSD([sQuery(id+"F0.wireOp",EDGE,"E3.0")])],"isStart":true});
            var Q4;
            Q4=makeQuery(id+"F1.opExtrude","CAP_EDGE",EDGE,{"disambiguationData":[OSD([sQuery(id+"F0.wireOp",EDGE,"E3.5")])],"isStart":true});
            var Q5;
            Q5=makeQuery(id+"F1.opExtrude","CAP_EDGE",EDGE,{"disambiguationData":[OSD([sQuery(id+"F0.wireOp",EDGE,"E10.2")])],"isStart":true});
            var Q6;
            Q6=makeQuery(id+"F1.opExtrude","CAP_EDGE",EDGE,{"disambiguationData":[OSD([sQuery(id+"F0.wireOp",EDGE,"E10.1")])],"isStart":true});
            var Q7;
            Q7=makeQuery(id+"F1.opExtrude","CAP_EDGE",EDGE,{"disambiguationData":[OSD([sQuery(id+"F0.wireOp",EDGE,"E10.0")])],"isStart":true});
            var Q8;
            Q8=makeQuery(id+"F1.opExtrude","CAP_EDGE",EDGE,{"disambiguationData":[OSD([sQuery(id+"F0.wireOp",EDGE,"E10.5")])],"isStart":true});
            var Q9;
            Q9=makeQuery(id+"F1.opExtrude","CAP_EDGE",EDGE,{"disambiguationData":[OSD([sQuery(id+"F0.wireOp",EDGE,"E2.2")])],"isStart":true});
            var Q10;
            Q10=makeQuery(id+"F1.opExtrude","CAP_EDGE",EDGE,{"disambiguationData":[OSD([sQuery(id+"F0.wireOp",EDGE,"E2.1")])],"isStart":true});
            var Q11;
            Q11=makeQuery(id+"F1.opExtrude","CAP_EDGE",EDGE,{"disambiguationData":[OSD([sQuery(id+"F0.wireOp",EDGE,"E2.0")])],"isStart":true});
            var Q12;
            Q12=makeQuery(id+"F1.opExtrude","CAP_EDGE",EDGE,{"disambiguationData":[OSD([sQuery(id+"F0.wireOp",EDGE,"E2.5")])],"isStart":true});
            var Q13;
            Q13=makeQuery(id+"F1.opExtrude","CAP_EDGE",EDGE,{"disambiguationData":[OSD([sQuery(id+"F0.wireOp",EDGE,"E9.0")])],"isStart":true});
            var Q14;
            Q14=makeQuery(id+"F1.opExtrude","CAP_EDGE",EDGE,{"disambiguationData":[OSD([sQuery(id+"F0.wireOp",EDGE,"E9.5")])],"isStart":true});
            var Q15;
            Q15=makeQuery(id+"F1.opExtrude","CAP_EDGE",EDGE,{"disambiguationData":[OSD([sQuery(id+"F0.wireOp",EDGE,"E9.4")])],"isStart":true});
            var Q16;
            Q16=makeQuery(id+"F1.opExtrude","CAP_EDGE",EDGE,{"disambiguationData":[OSD([sQuery(id+"F0.wireOp",EDGE,"E9.3")])],"isStart":true});
            var Q17;
            Q17=makeQuery(id+"F1.opExtrude","CAP_EDGE",EDGE,{"disambiguationData":[OSD([sQuery(id+"F0.wireOp",EDGE,"E1.0")])],"isStart":true});
            var Q18;
            Q18=makeQuery(id+"F1.opExtrude","CAP_EDGE",EDGE,{"disambiguationData":[OSD([sQuery(id+"F0.wireOp",EDGE,"E1.5")])],"isStart":true});
            var Q19;
            Q19=makeQuery(id+"F1.opExtrude","CAP_EDGE",EDGE,{"disambiguationData":[OSD([sQuery(id+"F0.wireOp",EDGE,"E1.4")])],"isStart":true});
            var Q20;
            Q20=makeQuery(id+"F1.opExtrude","CAP_EDGE",EDGE,{"disambiguationData":[OSD([sQuery(id+"F0.wireOp",EDGE,"E1.3")])],"isStart":true});
            var Q21;
            Q21=makeQuery(id+"F1.opExtrude","CAP_EDGE",EDGE,{"disambiguationData":[OSD([sQuery(id+"F0.wireOp",EDGE,"E11.2")])],"isStart":true});
            var Q22;
            Q22=makeQuery(id+"F1.opExtrude","CAP_EDGE",EDGE,{"disambiguationData":[OSD([sQuery(id+"F0.wireOp",EDGE,"E11.1")])],"isStart":true});
            var Q23;
            Q23=makeQuery(id+"F1.opExtrude","CAP_EDGE",EDGE,{"disambiguationData":[OSD([sQuery(id+"F0.wireOp",EDGE,"E11.0")])],"isStart":true});
            var Q24;
            Q24=makeQuery(id+"F1.opExtrude","CAP_EDGE",EDGE,{"disambiguationData":[OSD([sQuery(id+"F0.wireOp",EDGE,"E11.1")])],"isStart":false});
            var Q25;
            Q25=makeQuery(id+"F1.opExtrude","CAP_EDGE",EDGE,{"disambiguationData":[OSD([sQuery(id+"F0.wireOp",EDGE,"E11.0")])],"isStart":false});
            var Q26;
            Q26=makeQuery(id+"F1.opExtrude","CAP_EDGE",EDGE,{"disambiguationData":[OSD([sQuery(id+"F0.wireOp",EDGE,"E11.5")])],"isStart":false});
            var Q27;
            Q27=makeQuery(id+"F1.opExtrude","CAP_EDGE",EDGE,{"disambiguationData":[OSD([sQuery(id+"F0.wireOp",EDGE,"E3.2")])],"isStart":false});
            var Q28;
            Q28=makeQuery(id+"F1.opExtrude","CAP_EDGE",EDGE,{"disambiguationData":[OSD([sQuery(id+"F0.wireOp",EDGE,"E3.1")])],"isStart":false});
            var Q29;
            Q29=makeQuery(id+"F1.opExtrude","CAP_EDGE",EDGE,{"disambiguationData":[OSD([sQuery(id+"F0.wireOp",EDGE,"E3.0")])],"isStart":false});
            var Q30;
            Q30=makeQuery(id+"F1.opExtrude","CAP_EDGE",EDGE,{"disambiguationData":[OSD([sQuery(id+"F0.wireOp",EDGE,"E3.5")])],"isStart":false});
            var Q31;
            Q31=makeQuery(id+"F1.opExtrude","CAP_EDGE",EDGE,{"disambiguationData":[OSD([sQuery(id+"F0.wireOp",EDGE,"E10.2")])],"isStart":false});
            var Q32;
            Q32=makeQuery(id+"F1.opExtrude","CAP_EDGE",EDGE,{"disambiguationData":[OSD([sQuery(id+"F0.wireOp",EDGE,"E10.1")])],"isStart":false});
            var Q33;
            Q33=makeQuery(id+"F1.opExtrude","CAP_EDGE",EDGE,{"disambiguationData":[OSD([sQuery(id+"F0.wireOp",EDGE,"E10.0")])],"isStart":false});
            var Q34;
            Q34=makeQuery(id+"F1.opExtrude","CAP_EDGE",EDGE,{"disambiguationData":[OSD([sQuery(id+"F0.wireOp",EDGE,"E10.5")])],"isStart":false});
            var Q35;
            Q35=makeQuery(id+"F1.opExtrude","CAP_EDGE",EDGE,{"disambiguationData":[OSD([sQuery(id+"F0.wireOp",EDGE,"E2.2")])],"isStart":false});
            var Q36;
            Q36=makeQuery(id+"F1.opExtrude","CAP_EDGE",EDGE,{"disambiguationData":[OSD([sQuery(id+"F0.wireOp",EDGE,"E2.1")])],"isStart":false});
            var Q37;
            Q37=makeQuery(id+"F1.opExtrude","CAP_EDGE",EDGE,{"disambiguationData":[OSD([sQuery(id+"F0.wireOp",EDGE,"E2.0")])],"isStart":false});
            var Q38;
            Q38=makeQuery(id+"F1.opExtrude","CAP_EDGE",EDGE,{"disambiguationData":[OSD([sQuery(id+"F0.wireOp",EDGE,"E2.5")])],"isStart":false});
            var Q39;
            Q39=makeQuery(id+"F1.opExtrude","CAP_EDGE",EDGE,{"disambiguationData":[OSD([sQuery(id+"F0.wireOp",EDGE,"E9.0")])],"isStart":false});
            var Q40;
            Q40=makeQuery(id+"F1.opExtrude","CAP_EDGE",EDGE,{"disambiguationData":[OSD([sQuery(id+"F0.wireOp",EDGE,"E9.5")])],"isStart":false});
            var Q41;
            Q41=makeQuery(id+"F1.opExtrude","CAP_EDGE",EDGE,{"disambiguationData":[OSD([sQuery(id+"F0.wireOp",EDGE,"E1.0")])],"isStart":false});
            var Q42;
            Q42=makeQuery(id+"F1.opExtrude","CAP_EDGE",EDGE,{"disambiguationData":[OSD([sQuery(id+"F0.wireOp",EDGE,"E1.5")])],"isStart":false});
            var Q43;
            Q43=makeQuery(id+"F1.opExtrude","CAP_EDGE",EDGE,{"disambiguationData":[OSD([sQuery(id+"F0.wireOp",EDGE,"E1.4")])],"isStart":false});
            var Q44;
            Q44=makeQuery(id+"F1.opExtrude","CAP_EDGE",EDGE,{"disambiguationData":[OSD([sQuery(id+"F0.wireOp",EDGE,"E1.3")])],"isStart":false});
            var Q45;
            Q45=makeQuery(id+"F1.opExtrude","CAP_EDGE",EDGE,{"disambiguationData":[OSD([sQuery(id+"F0.wireOp",EDGE,"E11.2")])],"isStart":false});
            var Q46;
            Q46=makeQuery(id+"F1.opExtrude","CAP_EDGE",EDGE,{"disambiguationData":[OSD([sQuery(id+"F0.wireOp",EDGE,"E9.4")])],"isStart":false});
            var Q47;
            Q47=makeQuery(id+"F1.opExtrude","CAP_EDGE",EDGE,{"disambiguationData":[OSD([sQuery(id+"F0.wireOp",EDGE,"E9.3")])],"isStart":false});
            fillet(context, id + "F2", {"entities" : qUnion([Q0, Q1, Q2, Q3, Q4, Q5, Q6, Q7, Q8, Q9, Q10, Q11, Q12, Q13, Q14, Q15, Q16, Q17, Q18, Q19, Q20, Q21, Q22, Q23, Q24, Q25, Q26, Q27, Q28, Q29, Q30, Q31, Q32, Q33, Q34, Q35, Q36, Q37, Q38, Q39, Q40, Q41, Q42, Q43, Q44, Q45, Q46, Q47]), "radius" : 1.5 * mm, "tangentPropagation" : true, "allowEdgeOverflow" : false});
        }
    });
